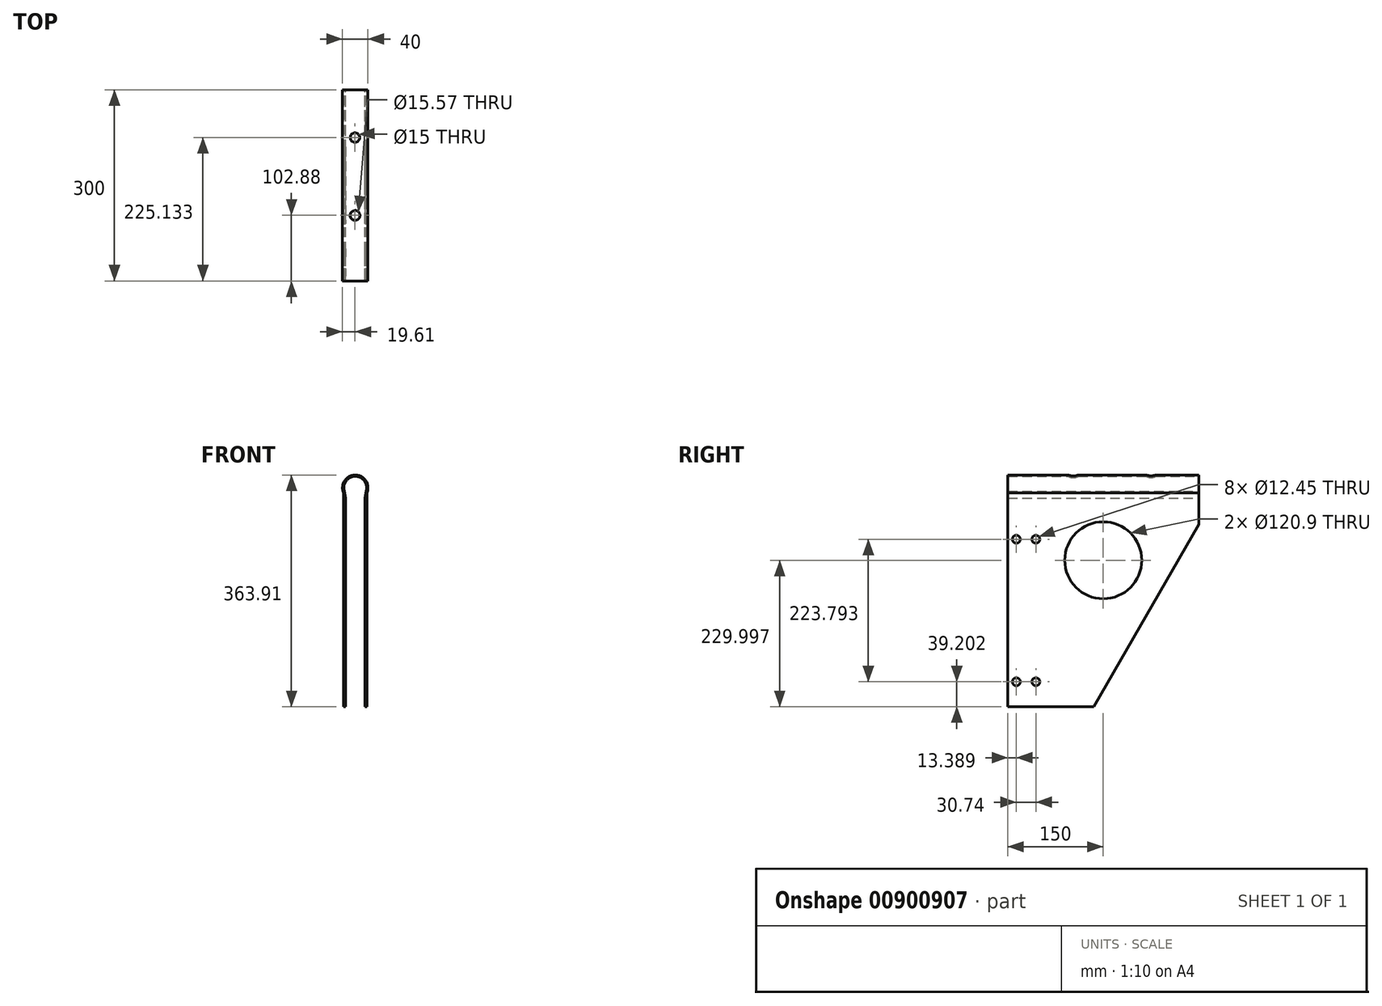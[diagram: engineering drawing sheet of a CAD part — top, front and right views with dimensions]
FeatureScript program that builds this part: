
annotation { "Feature Type Name" : "Feature", "Feature Type Description" : "" }
export const myFeature = defineFeature(function(context is Context, id is Id, definition is map)
    precondition{}
    {
        {
            var Q0;
            Q0=qCreatedBy(makeId("Front.planeOp"),FACE);
            var sketch = newSketch(context, id + "F0", { "sketchPlane" : qUnion([Q0])});
            skLineSegment(sketch, "E0", {"start": v(18.81, 86.41) * mm, "end": v(18.81, -257.5) * mm});
            skLineSegment(sketch, "E1", {"start": v(-18.04, 86.41) * mm, "end": v(-18.04, -257.5) * mm});
            skLineSegment(sketch, "E2", {"start": v(-18.04, -257.5) * mm, "end": v(18.81, -257.5) * mm});
            skPoint(sketch, "E3.end.orphan", {"position": v(-18.04, 0) * mm});
            skPoint(sketch, "E3.start.orphan", {"position": v(18.81, 0) * mm});
            skLineSegment(sketch, "E4", {"start": v(-18.04, 86.41) * mm, "end": v(18.81, 86.41) * mm});
            skPoint(sketch, "E5", {"position": v(0.39, 86.41) * mm});
            skCircle(sketch, "E6", {"center": v(0.39, 86.41) * mm, "radius": 20 * mm});
            skSolve(sketch);
        }
        {
            var Q0;
            Q0 = qSketchRegion(id + "F0", true);
            extrude(context, id + "F1", {"entities" : qUnion([Q0]), "depth" : 300 * mm, "offsetDistance" : 25 * mm});
        }
        {
            var Q0;
            Q0=makeQuery(id+"F1.opExtrude","CAP_FACE",FACE,{"disambiguationData":[OSD([sQuery(id+"F0.wireOp",EDGE,"E0"),sQuery(id+"F0.wireOp",EDGE,"E1"),sQuery(id+"F0.wireOp",EDGE,"E2"),sQuery(id+"F0.wireOp",EDGE,"AGc0xxmZ-yGO7-QFOc-dCNI-x4ArXhbZfAYx")])],"isStart":true});
            var sketch = newSketch(context, id + "F2", { "sketchPlane" : qUnion([Q0])});
            skLineSegment(sketch, "E7", {"start": v(174.27, 0) * mm, "end": v(174.27, -254.73) * mm});
            skLineSegment(sketch, "E8", {"start": v(174.27, -254.73) * mm, "end": v(174.27, 0) * mm});
            skLineSegment(sketch, "E9", {"start": v(174.27, 0) * mm, "end": v(174.27, 43.98) * mm});
            skLineSegment(sketch, "E10", {"start": v(174.27, 43.98) * mm, "end": v(174.27, 43.98) * mm});
            skPoint(sketch, "E11.start.orphan", {"position": v(0, -223.5) * mm});
            skLineSegment(sketch, "E12.left", {"start": v(174.27, -254.73) * mm, "end": v(174.27, -189.48) * mm});
            skPoint(sketch, "E12.right.end.orphan", {"position": v(-174.27, -189.48) * mm});
            skPoint(sketch, "E12.bottom.end.orphan", {"position": v(-174.27, -257.5) * mm});
            skPoint(sketch, "E13.orphan", {"position": v(174.27, -257.5) * mm});
            skLineSegment(sketch, "E14", {"start": v(174.27, -254.73) * mm, "end": v(174.27, -257.5) * mm});
            skLineSegment(sketch, "E15", {"start": v(174.27, -257.5) * mm, "end": v(174.27, -257.5) * mm});
            skLineSegment(sketch, "E16", {"start": v(174.27, -257.5) * mm, "end": v(174.27, -254.73) * mm});
            skArc(sketch, "E17", {"start": v(175.9, 44.7) * mm, "mid": v(159.72, 60.98) * mm, "end": v(143.53, 44.7) * mm});
            skLineSegment(sketch, "E18", {"start": v(175.9, 44.7) * mm, "end": v(174.26, 44.7) * mm});
            skLineSegment(sketch, "E19", {"start": v(143.53, 44.7) * mm, "end": v(145.34, 44.7) * mm});
            skCircle(sketch, "E20", {"center": v(159.72, 44.8) * mm, "radius": 16.17 * mm});
            skCircle(sketch, "E21", {"center": v(-0.39, 86.41) * mm, "radius": 17.92 * mm});
            skLineSegment(sketch, "E22.bottom", {"start": v(-0.39, 86.41) * mm, "end": v(-15.39, 86.41) * mm});
            skLineSegment(sketch, "E22.top", {"start": v(-0.39, -287.47) * mm, "end": v(-15.39, -287.47) * mm});
            skLineSegment(sketch, "E22.left", {"start": v(-0.39, 86.41) * mm, "end": v(-0.39, -287.47) * mm});
            skLineSegment(sketch, "E22.right", {"start": v(-15.39, 86.41) * mm, "end": v(-15.39, -287.47) * mm});
            skLineSegment(sketch, "E23.bottom", {"start": v(-0.39, 86.41) * mm, "end": v(14.61, 86.41) * mm});
            skLineSegment(sketch, "E23.top", {"start": v(-0.39, -287.47) * mm, "end": v(14.61, -287.47) * mm});
            skLineSegment(sketch, "E23.right", {"start": v(14.61, 86.41) * mm, "end": v(14.61, -287.47) * mm});
            skPoint(sketch, "E24", {"position": v(14.61, 73.37) * mm});
            skPoint(sketch, "E25", {"position": v(17.53, 86.41) * mm});
            skPoint(sketch, "E26", {"position": v(16.19, 79.6) * mm});
            skPoint(sketch, "E27", {"position": v(-18.3, 86.46) * mm});
            skPoint(sketch, "E28", {"position": v(-15.39, 72.9) * mm});
            skPoint(sketch, "E29", {"position": v(-16.96, 79.6) * mm});
            skSolve(sketch);
        }
        {
            var Q0;
            Q0 = qSketchRegion(id + "F2", true);
            extrude(context, id + "F3", {"entities" : qUnion([Q0]), "operationType" : NewBodyOperationType.REMOVE, "oppositeDirection" : true, "depth" : 300 * mm, "offsetDistance" : 25 * mm});
        }
        {
            var Q0;
            Q0=makeQuery(id+"F1.opExtrude","SWEPT_FACE",FACE,{"disambiguationData":[OSD([sQuery(id+"F0.wireOp",EDGE,"E0")])]});
            var sketch = newSketch(context, id + "F4", { "sketchPlane" : qUnion([Q0])});
            skPoint(sketch, "E30.center.orphan", {"position": v(-286.61, -218.3) * mm});
            skPoint(sketch, "E31.center.orphan", {"position": v(-293.48, -218.3) * mm});
            skPoint(sketch, "E32.center.orphan", {"position": v(-286.61, 5.5) * mm});
            skPoint(sketch, "E33.center.orphan", {"position": v(-293.48, 5.5) * mm});
            skCircle(sketch, "E34", {"center": v(-286.61, 5.5) * mm, "radius": 6.23 * mm});
            skPoint(sketch, "E35.center.orphan", {"position": v(-275.9, 5.5) * mm});
            skCircle(sketch, "E36", {"center": v(-255.87, 5.5) * mm, "radius": 6.23 * mm});
            skCircle(sketch, "E37", {"center": v(-255.87, -218.3) * mm, "radius": 6.23 * mm});
            skCircle(sketch, "E38", {"center": v(-286.61, -218.3) * mm, "radius": 6.23 * mm});
            skSolve(sketch);
        }
        {
            var Q0;
            Q0 = qSketchRegion(id + "F4", true);
            extrude(context, id + "F5", {"entities" : qUnion([Q0]), "operationType" : NewBodyOperationType.REMOVE, "oppositeDirection" : true, "depth" : 200 * mm, "offsetDistance" : 25 * mm});
        }
        {
            var Q0;
            Q0=qCreatedBy(makeId("Top.planeOp"),FACE);
            var sketch = newSketch(context, id + "F6", { "sketchPlane" : qUnion([Q0])});
            skCircle(sketch, "E39", {"center": v(0, -74.87) * mm, "radius": 7.5 * mm});
            skCircle(sketch, "E40", {"center": v(0, -197.12) * mm, "radius": 7.79 * mm});
            skSolve(sketch);
        }
        {
            var Q0;
            Q0 = qSketchRegion(id + "F6", true);
            extrude(context, id + "F7", {"entities" : qUnion([Q0]), "operationType" : NewBodyOperationType.REMOVE, "endBound" : BoundingType.THROUGH_ALL, "depth" : 25 * mm, "offsetDistance" : 25 * mm});
        }
        {
            var Q0;
            Q0=qCreatedBy(makeId("Front.planeOp"),FACE);
            var sketch = newSketch(context, id + "F8", { "sketchPlane" : qUnion([Q0])});
            skLineSegment(sketch, "E41", {"start": v(17.47, 81.28) * mm, "end": v(15.46, 69.9) * mm});
            skLineSegment(sketch, "E42", {"start": v(15.46, 69.9) * mm, "end": v(-14.6, 69.9) * mm});
            skLineSegment(sketch, "E43", {"start": v(-14.6, 69.9) * mm, "end": v(-16.7, 81.28) * mm});
            skLineSegment(sketch, "E44", {"start": v(-16.7, 81.28) * mm, "end": v(17.47, 81.28) * mm});
            skSolve(sketch);
        }
        {
            var Q0;
            Q0 = qSketchRegion(id + "F8", true);
            extrude(context, id + "F9", {"entities" : qUnion([Q0]), "operationType" : NewBodyOperationType.REMOVE, "depth" : 1000 * mm, "offsetDistance" : 25 * mm});
        }
        {
            var Q0;
            Q0=makeQuery(id+"F1.opExtrude","SWEPT_FACE",FACE,{"disambiguationData":[OSD([sQuery(id+"F0.wireOp",EDGE,"E0")])]});
            var sketch = newSketch(context, id + "F10", { "sketchPlane" : qUnion([Q0])});
            skLineSegment(sketch, "E45", {"start": v(-164.66, -257.5) * mm, "end": v(0, 28.77) * mm});
            skLineSegment(sketch, "E46", {"start": v(0, 28.77) * mm, "end": v(0, -257.5) * mm});
            skLineSegment(sketch, "E47", {"start": v(0, -257.5) * mm, "end": v(-164.66, -257.5) * mm});
            skCircle(sketch, "E48", {"center": v(-150, -27.5) * mm, "radius": 60.45 * mm});
            skSolve(sketch);
        }
        {
            var Q0;
            Q0 = qSketchRegion(id + "F10", true);
            extrude(context, id + "F11", {"entities" : qUnion([Q0]), "operationType" : NewBodyOperationType.REMOVE, "oppositeDirection" : true, "depth" : 500 * mm, "offsetDistance" : 25 * mm});
        }
    });
